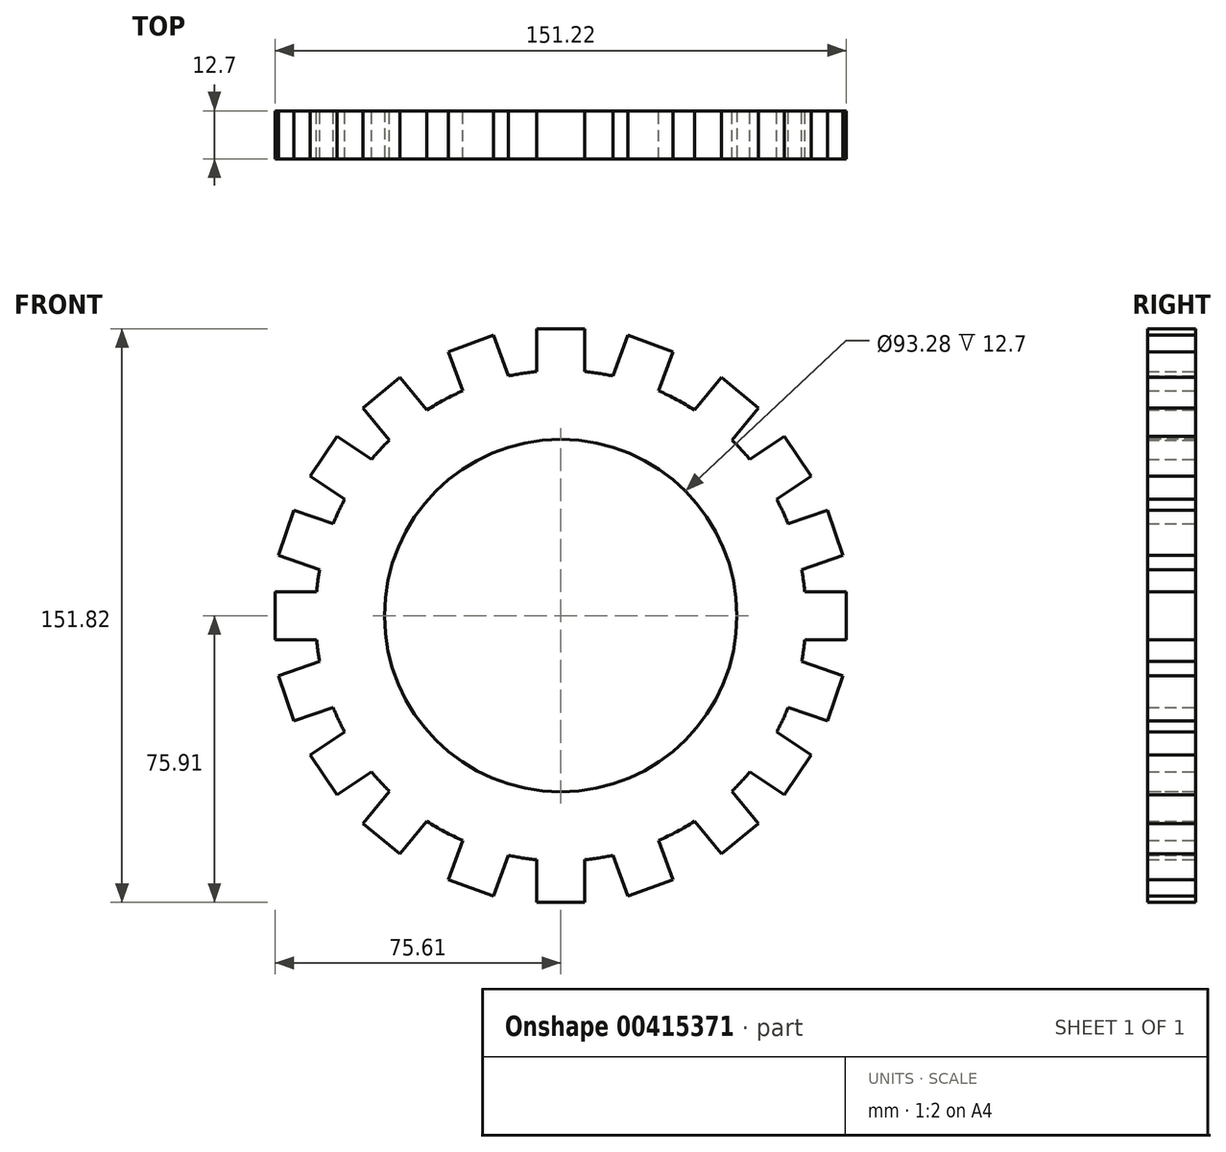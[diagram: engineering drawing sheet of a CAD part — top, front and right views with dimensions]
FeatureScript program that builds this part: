
annotation { "Feature Type Name" : "Feature", "Feature Type Description" : "" }
export const myFeature = defineFeature(function(context is Context, id is Id, definition is map)
    precondition{}
    {
        {
            var Q0;
            Q0=qCreatedBy(makeId("Front.planeOp"),FACE);
            var sketch = newSketch(context, id + "F0", { "sketchPlane" : qUnion([Q0])});
            skArc(sketch, "E0", {"start": v(-64.6, 6.35) * mm, "mid": v(-64.25, 9.27) * mm, "end": v(-63.77, 12.17) * mm});
            skLineSegment(sketch, "E1", {"start": v(-64.6, 6.35) * mm, "end": v(-75.6, 6.35) * mm});
            skLineSegment(sketch, "E2", {"start": v(-75.6, 6.35) * mm, "end": v(-75.6, 0) * mm});
            skLineSegment(sketch, "E3", {"start": v(-63.77, 12.17) * mm, "end": v(-74.69, 15.9) * mm});
            skLineSegment(sketch, "E4", {"start": v(-74.69, 15.9) * mm, "end": v(-70.58, 27.91) * mm});
            skLineSegment(sketch, "E5", {"start": v(-70.58, 27.91) * mm, "end": v(-60.17, 24.36) * mm});
            skArc(sketch, "E6.trimOffspring", {"start": v(-60.17, 24.36) * mm, "mid": v(-58.75, 27.61) * mm, "end": v(-57.15, 30.78) * mm});
            skLineSegment(sketch, "E7", {"start": v(-57.15, 30.78) * mm, "end": v(-66.28, 36.9) * mm});
            skLineSegment(sketch, "E8", {"start": v(-66.28, 36.9) * mm, "end": v(-59.2, 47.45) * mm});
            skLineSegment(sketch, "E9", {"start": v(-59.2, 47.45) * mm, "end": v(-50.07, 41.32) * mm});
            skArc(sketch, "E10.trimOffspring", {"start": v(-50.07, 41.32) * mm, "mid": v(-47.77, 43.96) * mm, "end": v(-45.33, 46.47) * mm});
            skLineSegment(sketch, "E11", {"start": v(-45.33, 46.47) * mm, "end": v(-52.3, 54.97) * mm});
            skLineSegment(sketch, "E12", {"start": v(-52.3, 54.97) * mm, "end": v(-42.48, 63.03) * mm});
            skLineSegment(sketch, "E13", {"start": v(-42.48, 63.03) * mm, "end": v(-35.41, 54.4) * mm});
            skArc(sketch, "E14.trimOffspring", {"start": v(-35.41, 54.4) * mm, "mid": v(-30.76, 57.16) * mm, "end": v(-25.9, 59.53) * mm});
            skLineSegment(sketch, "E15", {"start": v(-25.9, 59.53) * mm, "end": v(-29.68, 69.85) * mm});
            skLineSegment(sketch, "E16", {"start": v(-29.68, 69.85) * mm, "end": v(-17.76, 74.22) * mm});
            skLineSegment(sketch, "E17", {"start": v(-17.76, 74.22) * mm, "end": v(-13.8, 63.43) * mm});
            skArc(sketch, "E18.trimOffspring", {"start": v(-13.8, 63.43) * mm, "mid": v(-10.1, 64.13) * mm, "end": v(-6.35, 64.6) * mm});
            skLineSegment(sketch, "E19", {"start": v(-6.35, 75.91) * mm, "end": v(0, 75.91) * mm});
            skLineSegment(sketch, "E20.MirrorCS", {"start": v(-64.6, -6.35) * mm, "end": v(-75.6, -6.35) * mm});
            skLineSegment(sketch, "E21.MirrorCS", {"start": v(-63.77, -12.17) * mm, "end": v(-74.69, -15.9) * mm});
            skLineSegment(sketch, "E22.MirrorCS", {"start": v(-70.58, -27.91) * mm, "end": v(-60.17, -24.36) * mm});
            skLineSegment(sketch, "E23.MirrorCS", {"start": v(-74.69, -15.9) * mm, "end": v(-70.58, -27.91) * mm});
            skLineSegment(sketch, "E24.MirrorCS", {"start": v(-66.28, -36.9) * mm, "end": v(-59.2, -47.45) * mm});
            skLineSegment(sketch, "E25.MirrorCS", {"start": v(-52.3, -54.97) * mm, "end": v(-42.48, -63.03) * mm});
            skArc(sketch, "E26.MirrorCS", {"start": v(-35.41, -54.4) * mm, "mid": v(-30.76, -57.16) * mm, "end": v(-25.9, -59.53) * mm});
            skLineSegment(sketch, "E27.MirrorCS", {"start": v(-6.35, -75.91) * mm, "end": v(-6.35, -64.6) * mm});
            skLineSegment(sketch, "E28.MirrorCS", {"start": v(-17.76, -74.22) * mm, "end": v(-13.8, -63.43) * mm});
            skLineSegment(sketch, "E29.MirrorCS", {"start": v(-42.48, -63.03) * mm, "end": v(-35.41, -54.4) * mm});
            skLineSegment(sketch, "E30.MirrorCS", {"start": v(-45.33, -46.47) * mm, "end": v(-52.3, -54.97) * mm});
            skArc(sketch, "E31.MirrorCS", {"start": v(-50.07, -41.32) * mm, "mid": v(-47.77, -43.96) * mm, "end": v(-45.33, -46.47) * mm});
            skLineSegment(sketch, "E32.MirrorCS", {"start": v(-59.2, -47.45) * mm, "end": v(-50.07, -41.32) * mm});
            skLineSegment(sketch, "E33.MirrorCS", {"start": v(-57.15, -30.78) * mm, "end": v(-66.28, -36.9) * mm});
            skLineSegment(sketch, "E34.MirrorCS", {"start": v(-75.6, -6.35) * mm, "end": v(-75.6, 0) * mm});
            skArc(sketch, "E35.MirrorCS", {"start": v(-64.6, -6.35) * mm, "mid": v(-64.25, -9.27) * mm, "end": v(-63.77, -12.17) * mm});
            skArc(sketch, "E36.MirrorCS", {"start": v(-60.17, -24.36) * mm, "mid": v(-58.75, -27.61) * mm, "end": v(-57.15, -30.78) * mm});
            skLineSegment(sketch, "E37.MirrorCS", {"start": v(-6.35, -75.91) * mm, "end": v(0, -75.91) * mm});
            skLineSegment(sketch, "E38", {"start": v(-6.35, 75.91) * mm, "end": v(-6.35, 64.6) * mm});
            skArc(sketch, "E39.MirrorCS", {"start": v(-13.8, -63.43) * mm, "mid": v(-10.1, -64.13) * mm, "end": v(-6.35, -64.6) * mm});
            skLineSegment(sketch, "E40.MirrorCS", {"start": v(-29.68, -69.85) * mm, "end": v(-17.76, -74.22) * mm});
            skLineSegment(sketch, "E41.MirrorCS", {"start": v(-25.9, -59.53) * mm, "end": v(-29.68, -69.85) * mm});
            skLineSegment(sketch, "E42.MirrorCS", {"start": v(6.35, 75.91) * mm, "end": v(0, 75.91) * mm});
            skLineSegment(sketch, "E43.MirrorCS", {"start": v(6.35, 75.91) * mm, "end": v(6.35, 64.6) * mm});
            skArc(sketch, "E44.MirrorCS", {"start": v(13.8, 63.43) * mm, "mid": v(10.1, 64.13) * mm, "end": v(6.35, 64.6) * mm});
            skLineSegment(sketch, "E45.MirrorCS", {"start": v(17.76, 74.22) * mm, "end": v(13.8, 63.43) * mm});
            skLineSegment(sketch, "E46.MirrorCS", {"start": v(25.9, 59.53) * mm, "end": v(29.68, 69.85) * mm});
            skLineSegment(sketch, "E47.MirrorCS", {"start": v(29.68, 69.85) * mm, "end": v(17.76, 74.22) * mm});
            skLineSegment(sketch, "E48.MirrorCS", {"start": v(42.48, 63.03) * mm, "end": v(35.41, 54.4) * mm});
            skArc(sketch, "E49.MirrorCS", {"start": v(35.41, 54.4) * mm, "mid": v(30.76, 57.16) * mm, "end": v(25.9, 59.53) * mm});
            skLineSegment(sketch, "E50.MirrorCS", {"start": v(52.3, 54.97) * mm, "end": v(42.48, 63.03) * mm});
            skLineSegment(sketch, "E51.MirrorCS", {"start": v(45.33, 46.47) * mm, "end": v(52.3, 54.97) * mm});
            skLineSegment(sketch, "E52.MirrorCS", {"start": v(59.2, 47.45) * mm, "end": v(50.07, 41.32) * mm});
            skArc(sketch, "E53.MirrorCS", {"start": v(50.07, 41.32) * mm, "mid": v(47.77, 43.96) * mm, "end": v(45.33, 46.47) * mm});
            skLineSegment(sketch, "E54.MirrorCS", {"start": v(66.28, 36.9) * mm, "end": v(59.2, 47.45) * mm});
            skLineSegment(sketch, "E55.MirrorCS", {"start": v(57.15, 30.78) * mm, "end": v(66.28, 36.9) * mm});
            skArc(sketch, "E56.MirrorCS", {"start": v(60.17, 24.36) * mm, "mid": v(58.75, 27.61) * mm, "end": v(57.15, 30.78) * mm});
            skLineSegment(sketch, "E57.MirrorCS", {"start": v(74.69, 15.9) * mm, "end": v(70.58, 27.91) * mm});
            skLineSegment(sketch, "E58.MirrorCS", {"start": v(70.58, 27.91) * mm, "end": v(60.17, 24.36) * mm});
            skLineSegment(sketch, "E59.MirrorCS", {"start": v(63.77, 12.17) * mm, "end": v(74.69, 15.9) * mm});
            skArc(sketch, "E60.MirrorCS", {"start": v(64.6, 6.35) * mm, "mid": v(64.25, 9.27) * mm, "end": v(63.77, 12.17) * mm});
            skLineSegment(sketch, "E61.MirrorCS", {"start": v(64.6, 6.35) * mm, "end": v(75.6, 6.35) * mm});
            skLineSegment(sketch, "E62.MirrorCS", {"start": v(75.6, 6.35) * mm, "end": v(75.6, 0) * mm});
            skLineSegment(sketch, "E63.MirrorCS", {"start": v(64.6, -6.35) * mm, "end": v(75.6, -6.35) * mm});
            skLineSegment(sketch, "E64.MirrorCS", {"start": v(75.6, -6.35) * mm, "end": v(75.6, 0) * mm});
            skArc(sketch, "E65.MirrorCS", {"start": v(64.6, -6.35) * mm, "mid": v(64.25, -9.27) * mm, "end": v(63.77, -12.17) * mm});
            skLineSegment(sketch, "E66.MirrorCS", {"start": v(63.77, -12.17) * mm, "end": v(74.69, -15.9) * mm});
            skLineSegment(sketch, "E67.MirrorCS", {"start": v(74.69, -15.9) * mm, "end": v(70.58, -27.91) * mm});
            skLineSegment(sketch, "E68.MirrorCS", {"start": v(70.58, -27.91) * mm, "end": v(60.17, -24.36) * mm});
            skArc(sketch, "E69.MirrorCS", {"start": v(60.17, -24.36) * mm, "mid": v(58.75, -27.61) * mm, "end": v(57.15, -30.78) * mm});
            skLineSegment(sketch, "E70.MirrorCS", {"start": v(57.15, -30.78) * mm, "end": v(66.28, -36.9) * mm});
            skLineSegment(sketch, "E71.MirrorCS", {"start": v(66.28, -36.9) * mm, "end": v(59.2, -47.45) * mm});
            skLineSegment(sketch, "E72.MirrorCS", {"start": v(59.2, -47.45) * mm, "end": v(50.07, -41.32) * mm});
            skArc(sketch, "E73.MirrorCS", {"start": v(50.07, -41.32) * mm, "mid": v(47.77, -43.96) * mm, "end": v(45.33, -46.47) * mm});
            skLineSegment(sketch, "E74.MirrorCS", {"start": v(45.33, -46.47) * mm, "end": v(52.3, -54.97) * mm});
            skLineSegment(sketch, "E75.MirrorCS", {"start": v(52.3, -54.97) * mm, "end": v(42.48, -63.03) * mm});
            skLineSegment(sketch, "E76.MirrorCS", {"start": v(42.48, -63.03) * mm, "end": v(35.41, -54.4) * mm});
            skArc(sketch, "E77.MirrorCS", {"start": v(35.41, -54.4) * mm, "mid": v(30.76, -57.16) * mm, "end": v(25.9, -59.53) * mm});
            skLineSegment(sketch, "E78.MirrorCS", {"start": v(25.9, -59.53) * mm, "end": v(29.68, -69.85) * mm});
            skLineSegment(sketch, "E79.MirrorCS", {"start": v(29.68, -69.85) * mm, "end": v(17.76, -74.22) * mm});
            skLineSegment(sketch, "E80.MirrorCS", {"start": v(17.76, -74.22) * mm, "end": v(13.8, -63.43) * mm});
            skArc(sketch, "E81.MirrorCS", {"start": v(13.8, -63.43) * mm, "mid": v(10.1, -64.13) * mm, "end": v(6.35, -64.6) * mm});
            skLineSegment(sketch, "E82.MirrorCS", {"start": v(6.35, -75.91) * mm, "end": v(6.35, -64.6) * mm});
            skLineSegment(sketch, "E83.MirrorCS", {"start": v(6.35, -75.91) * mm, "end": v(0, -75.91) * mm});
            skSolve(sketch);
        }
        {
            var Q0;
            Q0 = qSketchRegion(id + "F0", true);
            extrude(context, id + "F1", {"entities" : qUnion([Q0]), "depth" : 12.7 * mm});
        }
        {
            var Q0;
            Q0=makeQuery(id+"F1.opExtrude","CAP_FACE",FACE,{"disambiguationData":[OSD([sQuery(id+"F0.wireOp",EDGE,"E0"),sQuery(id+"F0.wireOp",EDGE,"E1"),sQuery(id+"F0.wireOp",EDGE,"E2"),sQuery(id+"F0.wireOp",EDGE,"E3"),sQuery(id+"F0.wireOp",EDGE,"E4"),sQuery(id+"F0.wireOp",EDGE,"E5"),sQuery(id+"F0.wireOp",EDGE,"E6.trimOffspring"),sQuery(id+"F0.wireOp",EDGE,"E7"),sQuery(id+"F0.wireOp",EDGE,"E8"),sQuery(id+"F0.wireOp",EDGE,"E9"),sQuery(id+"F0.wireOp",EDGE,"E10.trimOffspring"),sQuery(id+"F0.wireOp",EDGE,"E11"),sQuery(id+"F0.wireOp",EDGE,"E12"),sQuery(id+"F0.wireOp",EDGE,"E13"),sQuery(id+"F0.wireOp",EDGE,"E14.trimOffspring"),sQuery(id+"F0.wireOp",EDGE,"E15"),sQuery(id+"F0.wireOp",EDGE,"E16"),sQuery(id+"F0.wireOp",EDGE,"E17"),sQuery(id+"F0.wireOp",EDGE,"E18.trimOffspring"),sQuery(id+"F0.wireOp",EDGE,"E19"),sQuery(id+"F0.wireOp",EDGE,"E21.MirrorCS"),sQuery(id+"F0.wireOp",EDGE,"E22.MirrorCS"),sQuery(id+"F0.wireOp",EDGE,"E23.MirrorCS"),sQuery(id+"F0.wireOp",EDGE,"E24.MirrorCS"),sQuery(id+"F0.wireOp",EDGE,"E27.MirrorCS"),sQuery(id+"F0.wireOp",EDGE,"E25.MirrorCS"),sQuery(id+"F0.wireOp",EDGE,"E29.MirrorCS"),sQuery(id+"F0.wireOp",EDGE,"E30.MirrorCS"),sQuery(id+"F0.wireOp",EDGE,"E31.MirrorCS"),sQuery(id+"F0.wireOp",EDGE,"E32.MirrorCS"),sQuery(id+"F0.wireOp",EDGE,"E33.MirrorCS"),sQuery(id+"F0.wireOp",EDGE,"E20.MirrorCS"),sQuery(id+"F0.wireOp",EDGE,"E34.MirrorCS"),sQuery(id+"F0.wireOp",EDGE,"E35.MirrorCS"),sQuery(id+"F0.wireOp",EDGE,"E36.MirrorCS"),sQuery(id+"F0.wireOp",EDGE,"E37.MirrorCS"),sQuery(id+"F0.wireOp",EDGE,"E38"),sQuery(id+"F0.wireOp",EDGE,"E39.MirrorCS"),sQuery(id+"F0.wireOp",EDGE,"E28.MirrorCS"),sQuery(id+"F0.wireOp",EDGE,"E40.MirrorCS"),sQuery(id+"F0.wireOp",EDGE,"E41.MirrorCS"),sQuery(id+"F0.wireOp",EDGE,"E26.MirrorCS"),sQuery(id+"F0.wireOp",EDGE,"E42.MirrorCS"),sQuery(id+"F0.wireOp",EDGE,"E43.MirrorCS"),sQuery(id+"F0.wireOp",EDGE,"E44.MirrorCS"),sQuery(id+"F0.wireOp",EDGE,"E45.MirrorCS"),sQuery(id+"F0.wireOp",EDGE,"E46.MirrorCS"),sQuery(id+"F0.wireOp",EDGE,"E47.MirrorCS"),sQuery(id+"F0.wireOp",EDGE,"E48.MirrorCS"),sQuery(id+"F0.wireOp",EDGE,"E49.MirrorCS"),sQuery(id+"F0.wireOp",EDGE,"E50.MirrorCS"),sQuery(id+"F0.wireOp",EDGE,"E51.MirrorCS"),sQuery(id+"F0.wireOp",EDGE,"E52.MirrorCS"),sQuery(id+"F0.wireOp",EDGE,"E53.MirrorCS"),sQuery(id+"F0.wireOp",EDGE,"E54.MirrorCS"),sQuery(id+"F0.wireOp",EDGE,"E55.MirrorCS"),sQuery(id+"F0.wireOp",EDGE,"E56.MirrorCS"),sQuery(id+"F0.wireOp",EDGE,"E57.MirrorCS"),sQuery(id+"F0.wireOp",EDGE,"E58.MirrorCS"),sQuery(id+"F0.wireOp",EDGE,"E59.MirrorCS"),sQuery(id+"F0.wireOp",EDGE,"E60.MirrorCS"),sQuery(id+"F0.wireOp",EDGE,"E61.MirrorCS"),sQuery(id+"F0.wireOp",EDGE,"E62.MirrorCS"),sQuery(id+"F0.wireOp",EDGE,"E63.MirrorCS"),sQuery(id+"F0.wireOp",EDGE,"E64.MirrorCS"),sQuery(id+"F0.wireOp",EDGE,"E65.MirrorCS"),sQuery(id+"F0.wireOp",EDGE,"E66.MirrorCS"),sQuery(id+"F0.wireOp",EDGE,"E67.MirrorCS"),sQuery(id+"F0.wireOp",EDGE,"E68.MirrorCS"),sQuery(id+"F0.wireOp",EDGE,"E69.MirrorCS"),sQuery(id+"F0.wireOp",EDGE,"E70.MirrorCS"),sQuery(id+"F0.wireOp",EDGE,"E71.MirrorCS"),sQuery(id+"F0.wireOp",EDGE,"E72.MirrorCS"),sQuery(id+"F0.wireOp",EDGE,"E73.MirrorCS"),sQuery(id+"F0.wireOp",EDGE,"E74.MirrorCS"),sQuery(id+"F0.wireOp",EDGE,"E75.MirrorCS"),sQuery(id+"F0.wireOp",EDGE,"E76.MirrorCS"),sQuery(id+"F0.wireOp",EDGE,"E77.MirrorCS"),sQuery(id+"F0.wireOp",EDGE,"E78.MirrorCS"),sQuery(id+"F0.wireOp",EDGE,"E79.MirrorCS"),sQuery(id+"F0.wireOp",EDGE,"E80.MirrorCS"),sQuery(id+"F0.wireOp",EDGE,"E81.MirrorCS"),sQuery(id+"F0.wireOp",EDGE,"E82.MirrorCS"),sQuery(id+"F0.wireOp",EDGE,"E83.MirrorCS")])],"isStart":false});
            var sketch = newSketch(context, id + "F2", { "sketchPlane" : qUnion([Q0])});
            skLineSegment(sketch, "E84", {"start": v(0, 90.74) * mm, "end": v(0, -98.96) * mm, "construction": true});
            skPoint(sketch, "E84.startSnap0", {"position": v(0, 75.91) * mm});
            skPoint(sketch, "E84.endSnap0", {"position": v(0, -75.91) * mm});
            skLineSegment(sketch, "E85", {"start": v(-98.44, 0) * mm, "end": v(106.94, 0) * mm, "construction": true});
            skCircle(sketch, "E86", {"center": v(0, 0) * mm, "radius": 46.64 * mm});
            skSolve(sketch);
        }
        {
            var Q0;
            Q0 = qSketchRegion(id + "F2", true);
            extrude(context, id + "F3", {"entities" : qUnion([Q0]), "operationType" : NewBodyOperationType.REMOVE, "oppositeDirection" : true, "depth" : 25.4 * mm});
        }
    });
